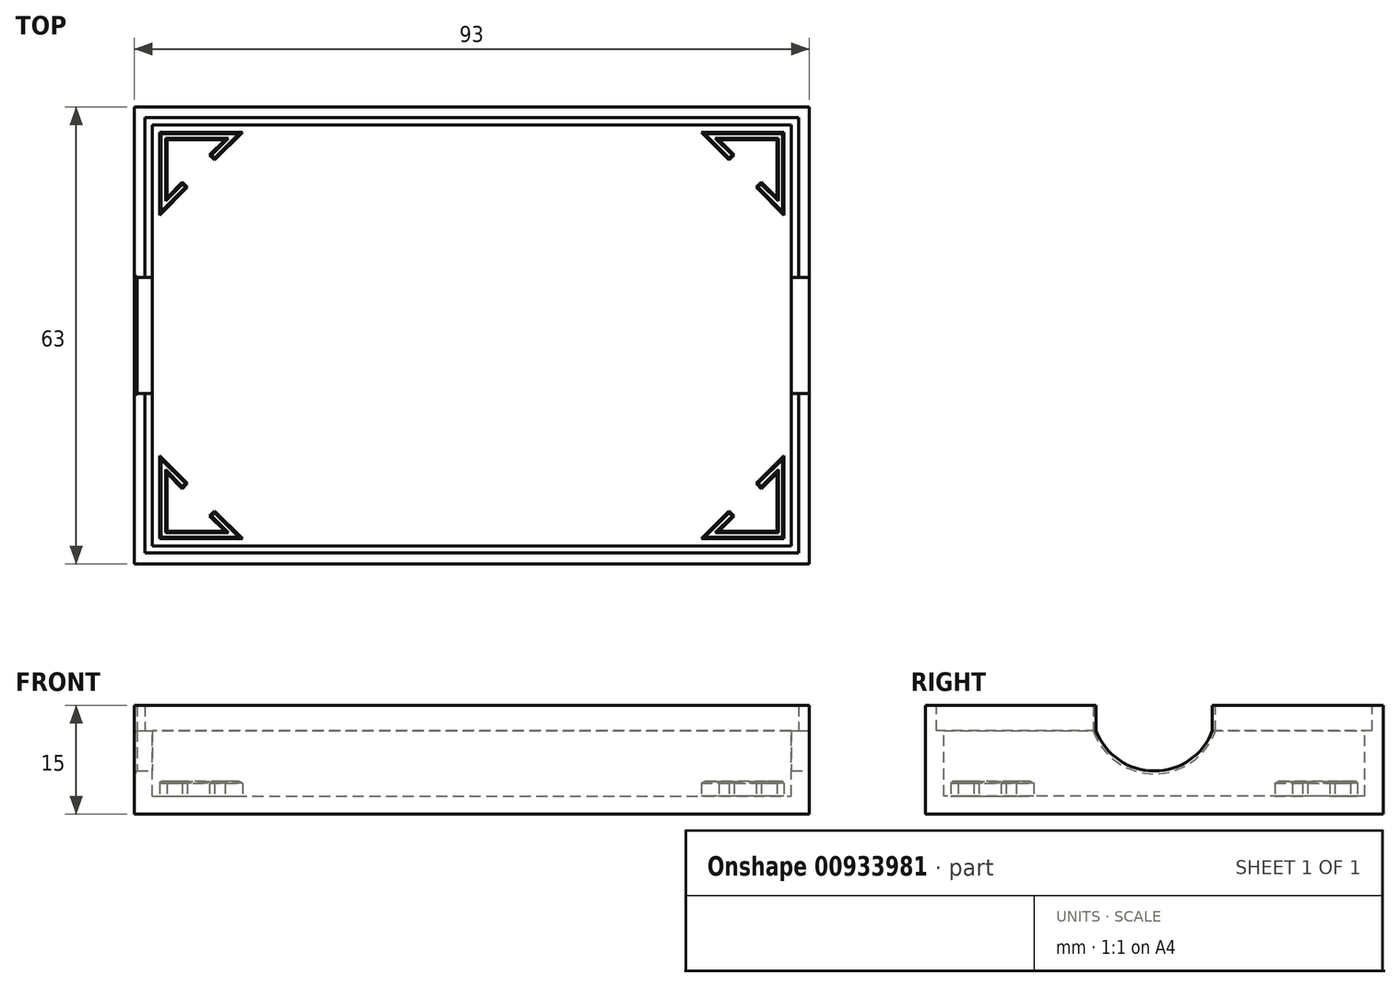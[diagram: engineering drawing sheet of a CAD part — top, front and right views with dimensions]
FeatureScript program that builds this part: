
annotation { "Feature Type Name" : "Feature", "Feature Type Description" : "" }
export const myFeature = defineFeature(function(context is Context, id is Id, definition is map)
    precondition{}
    {
        {
            var Q0;
            Q0=qCreatedBy(makeId("Top.planeOp"),FACE);
            var sketch = newSketch(context, id + "F0", { "sketchPlane" : qUnion([Q0])});
            skLineSegment(sketch, "E0.0", {"start": v(46.5, 31.5) * mm, "end": v(46.5, -31.5) * mm});
            skLineSegment(sketch, "E0.1", {"start": v(-46.5, 31.5) * mm, "end": v(46.5, 31.5) * mm});
            skLineSegment(sketch, "E0.2", {"start": v(-46.5, 31.5) * mm, "end": v(-46.5, -31.5) * mm});
            skLineSegment(sketch, "E0.3", {"start": v(-46.5, -31.5) * mm, "end": v(46.5, -31.5) * mm});
            skPoint(sketch, "E1", {"position": v(0, 31.5) * mm});
            skPoint(sketch, "E2", {"position": v(46.5, 0) * mm});
            skSolve(sketch);
        }
        {
            var Q0;
            Q0 = qSketchRegion(id + "F0", true);
            extrude(context, id + "F1", {"entities" : qUnion([Q0]), "oppositeDirection" : true, "depth" : 15 * mm, "offsetDistance" : 25 * mm});
        }
        {
            var Q0;
            Q0=makeQuery(id+"F1.opExtrude","CAP_FACE",FACE,{"disambiguationData":[OSD([sQuery(id+"F0.wireOp",EDGE,"E0.0"),sQuery(id+"F0.wireOp",EDGE,"E0.1"),sQuery(id+"F0.wireOp",EDGE,"E0.2"),sQuery(id+"F0.wireOp",EDGE,"E0.3")])],"isStart":true});
            shell(context, id + "F2", {"entities" : qUnion([Q0]), "thickness" : 2.5 * mm});
        }
        {
            var Q0;
            Q0=qCreatedBy(makeId("Top.planeOp"),FACE);
            var sketch = newSketch(context, id + "F3", { "sketchPlane" : qUnion([Q0])});
            skLineSegment(sketch, "E3.bottom", {"start": v(-45, 30) * mm, "end": v(45, 30) * mm});
            skLineSegment(sketch, "E3.top", {"start": v(-45, -30) * mm, "end": v(45, -30) * mm});
            skLineSegment(sketch, "E3.left", {"start": v(-45, 30) * mm, "end": v(-45, -30) * mm});
            skLineSegment(sketch, "E3.right", {"start": v(45, 30) * mm, "end": v(45, -30) * mm});
            skPoint(sketch, "E4", {"position": v(0, 30) * mm});
            skPoint(sketch, "E5", {"position": v(45, 0) * mm});
            skSolve(sketch);
        }
        {
            var Q0;
            Q0 = qSketchRegion(id + "F3", true);
            extrude(context, id + "F4", {"entities" : qUnion([Q0]), "operationType" : NewBodyOperationType.REMOVE, "oppositeDirection" : true, "depth" : 3.5 * mm, "offsetDistance" : 25 * mm});
        }
        {
            var Q0;
            Q0=makeQuery(id+"F2.opShell","OFFSET_FACE",FACE,{"disambiguationData":[OSD([sQuery(id+"F0.wireOp",EDGE,"E0.0"),sQuery(id+"F0.wireOp",EDGE,"E0.1"),sQuery(id+"F0.wireOp",EDGE,"E0.2"),sQuery(id+"F0.wireOp",EDGE,"E0.3")])]});
            var sketch = newSketch(context, id + "F5", { "sketchPlane" : qUnion([Q0])});
            skLineSegment(sketch, "E6.bottom", {"start": v(-42, 27) * mm, "end": v(-34, 27) * mm});
            skLineSegment(sketch, "E6.left", {"start": v(-42, 27) * mm, "end": v(-42, 19) * mm});
            skLineSegment(sketch, "E7", {"start": v(-42, 19) * mm, "end": v(-39.88, 21.12) * mm});
            skLineSegment(sketch, "E8.0", {"start": v(-43, 16.59) * mm, "end": v(-39.17, 20.41) * mm});
            skLineSegment(sketch, "E8.1", {"start": v(-43, 28) * mm, "end": v(-43, 16.59) * mm});
            skLineSegment(sketch, "E8.2", {"start": v(-43, 28) * mm, "end": v(-31.59, 28) * mm});
            skLineSegment(sketch, "E9.MirrorCS", {"start": v(42, 27) * mm, "end": v(34, 27) * mm});
            skLineSegment(sketch, "E10.MirrorCS", {"start": v(42, 27) * mm, "end": v(42, 19) * mm});
            skLineSegment(sketch, "E11.MirrorCS", {"start": v(43, 28) * mm, "end": v(43, 16.59) * mm});
            skLineSegment(sketch, "E12.MirrorCS", {"start": v(43, 28) * mm, "end": v(31.59, 28) * mm});
            skLineSegment(sketch, "E13.MirrorCS", {"start": v(-43, -28) * mm, "end": v(-31.59, -28) * mm});
            skLineSegment(sketch, "E14.MirrorCS", {"start": v(-42, -27) * mm, "end": v(-34, -27) * mm});
            skLineSegment(sketch, "E15.MirrorCS", {"start": v(-42, -27) * mm, "end": v(-42, -19) * mm});
            skLineSegment(sketch, "E16.MirrorCS", {"start": v(-43, -28) * mm, "end": v(-43, -16.59) * mm});
            skLineSegment(sketch, "E17.MirrorCS", {"start": v(43, -28) * mm, "end": v(31.59, -28) * mm});
            skLineSegment(sketch, "E18.MirrorCS", {"start": v(43, -28) * mm, "end": v(43, -16.59) * mm});
            skLineSegment(sketch, "E19.MirrorCS", {"start": v(42, -27) * mm, "end": v(42, -19) * mm});
            skLineSegment(sketch, "E20.MirrorCS", {"start": v(42, -27) * mm, "end": v(34, -27) * mm});
            skLineSegment(sketch, "E21", {"start": v(-39.88, 21.12) * mm, "end": v(-39.17, 20.41) * mm});
            skLineSegment(sketch, "E22", {"start": v(-36.12, 24.88) * mm, "end": v(-35.41, 24.17) * mm});
            skLineSegment(sketch, "E23.trimOffspring", {"start": v(-35.41, 24.17) * mm, "end": v(-31.59, 28) * mm});
            skLineSegment(sketch, "E24.trimOffspring", {"start": v(-36.12, 24.88) * mm, "end": v(-34, 27) * mm});
            skLineSegment(sketch, "E25.MirrorCS", {"start": v(35.41, 24.17) * mm, "end": v(31.59, 28) * mm});
            skLineSegment(sketch, "E26.MirrorCS", {"start": v(36.12, 24.88) * mm, "end": v(34, 27) * mm});
            skLineSegment(sketch, "E27.MirrorCS", {"start": v(36.12, 24.88) * mm, "end": v(35.41, 24.17) * mm});
            skLineSegment(sketch, "E28.MirrorCS", {"start": v(39.88, 21.12) * mm, "end": v(39.17, 20.41) * mm});
            skLineSegment(sketch, "E29.MirrorCS", {"start": v(42, 19) * mm, "end": v(39.88, 21.12) * mm});
            skLineSegment(sketch, "E30.MirrorCS", {"start": v(43, 16.59) * mm, "end": v(39.17, 20.41) * mm});
            skLineSegment(sketch, "E31.MirrorCS", {"start": v(-42, -19) * mm, "end": v(-39.88, -21.12) * mm});
            skLineSegment(sketch, "E32.MirrorCS", {"start": v(-39.88, -21.12) * mm, "end": v(-39.17, -20.41) * mm});
            skLineSegment(sketch, "E33.MirrorCS", {"start": v(-43, -16.59) * mm, "end": v(-39.17, -20.41) * mm});
            skLineSegment(sketch, "E34.MirrorCS", {"start": v(-36.12, -24.88) * mm, "end": v(-34, -27) * mm});
            skLineSegment(sketch, "E35.MirrorCS", {"start": v(-36.12, -24.88) * mm, "end": v(-35.41, -24.17) * mm});
            skLineSegment(sketch, "E36.MirrorCS", {"start": v(-35.41, -24.17) * mm, "end": v(-31.59, -28) * mm});
            skLineSegment(sketch, "E37.MirrorCS", {"start": v(42, -19) * mm, "end": v(39.88, -21.12) * mm});
            skLineSegment(sketch, "E38.MirrorCS", {"start": v(39.88, -21.12) * mm, "end": v(39.17, -20.41) * mm});
            skLineSegment(sketch, "E39.MirrorCS", {"start": v(43, -16.59) * mm, "end": v(39.17, -20.41) * mm});
            skLineSegment(sketch, "E40.MirrorCS", {"start": v(36.12, -24.88) * mm, "end": v(34, -27) * mm});
            skLineSegment(sketch, "E41.MirrorCS", {"start": v(35.41, -24.17) * mm, "end": v(31.59, -28) * mm});
            skLineSegment(sketch, "E42.MirrorCS", {"start": v(36.12, -24.88) * mm, "end": v(35.41, -24.17) * mm});
            skSolve(sketch);
        }
        {
            var Q0;
            Q0 = qSketchRegion(id + "F5", true);
            extrude(context, id + "F6", {"entities" : qUnion([Q0]), "operationType" : NewBodyOperationType.ADD, "depth" : 2 * mm, "offsetDistance" : 25 * mm});
        }
        {
            var Q0;
            Q0=makeQuery(id+"F6.opExtrude","CAP_FACE",FACE,{"disambiguationData":[OSD([sQuery(id+"F5.wireOp",EDGE,"E6.bottom"),sQuery(id+"F5.wireOp",EDGE,"E6.left"),sQuery(id+"F5.wireOp",EDGE,"E7"),sQuery(id+"F5.wireOp",EDGE,"E8.0"),sQuery(id+"F5.wireOp",EDGE,"E8.1"),sQuery(id+"F5.wireOp",EDGE,"E8.2")])],"isStart":false});
            var Q1;
            Q1=makeQuery(id+"F6.opExtrude","CAP_FACE",FACE,{"disambiguationData":[OSD([sQuery(id+"F5.wireOp",EDGE,"7368ef62-361c-4206-994a-d8a41f0acc9b0.MirrorCS"),sQuery(id+"F5.wireOp",EDGE,"065983df-0b87-484f-8e97-a6bd623cd0b60.MirrorCS"),sQuery(id+"F5.wireOp",EDGE,"E9.MirrorCS"),sQuery(id+"F5.wireOp",EDGE,"E10.MirrorCS"),sQuery(id+"F5.wireOp",EDGE,"E11.MirrorCS"),sQuery(id+"F5.wireOp",EDGE,"E12.MirrorCS")])],"isStart":false});
            var Q2;
            Q2=makeQuery(id+"F6.opExtrude","CAP_FACE",FACE,{"disambiguationData":[OSD([sQuery(id+"F5.wireOp",EDGE,"cfee1d1f-dcdf-40e0-b635-4211958b80790.MirrorCS"),sQuery(id+"F5.wireOp",EDGE,"2ad0a4fe-2727-4fc3-9ba8-781443fbefe10.MirrorCS"),sQuery(id+"F5.wireOp",EDGE,"E17.MirrorCS"),sQuery(id+"F5.wireOp",EDGE,"E18.MirrorCS"),sQuery(id+"F5.wireOp",EDGE,"E19.MirrorCS"),sQuery(id+"F5.wireOp",EDGE,"E20.MirrorCS")])],"isStart":false});
            var Q3;
            Q3=makeQuery(id+"F6.opExtrude","CAP_FACE",FACE,{"disambiguationData":[OSD([sQuery(id+"F5.wireOp",EDGE,"E13.MirrorCS"),sQuery(id+"F5.wireOp",EDGE,"E14.MirrorCS"),sQuery(id+"F5.wireOp",EDGE,"E15.MirrorCS"),sQuery(id+"F5.wireOp",EDGE,"E16.MirrorCS"),sQuery(id+"F5.wireOp",EDGE,"85b368af-3590-4ccb-beb0-d535ae87f27b0.MirrorCS"),sQuery(id+"F5.wireOp",EDGE,"bbde580a-0e57-42fd-9440-816c3c4a825d0.MirrorCS")])],"isStart":false});
            chamfer(context, id + "F7", {"entities" : qUnion([Q0, Q1, Q2, Q3]), "width" : 0.2 * mm, "tangentPropagation" : true});
        }
        {
            var Q0;
            Q0=makeQuery(id+"F1.opExtrude","SWEPT_FACE",FACE,{"disambiguationData":[OSD([sQuery(id+"F0.wireOp",EDGE,"E0.0")])]});
            var sketch = newSketch(context, id + "F8", { "sketchPlane" : qUnion([Q0])});
            skPoint(sketch, "E43", {"position": v(-8, 0) * mm});
            skPoint(sketch, "E44", {"position": v(8, 0) * mm});
            skPoint(sketch, "E45", {"position": v(-8, -3.5) * mm});
            skPoint(sketch, "E46", {"position": v(8, -3.5) * mm});
            skArc(sketch, "E47", {"start": v(-8, -3.5) * mm, "mid": v(0, -9.04) * mm, "end": v(8, -3.5) * mm});
            skLineSegment(sketch, "E48", {"start": v(-8, 0) * mm, "end": v(0, 0) * mm});
            skLineSegment(sketch, "E49", {"start": v(0, 0) * mm, "end": v(8, 0) * mm});
            skLineSegment(sketch, "E50", {"start": v(8, -3.5) * mm, "end": v(8, 0) * mm});
            skLineSegment(sketch, "E51", {"start": v(-8, 0) * mm, "end": v(-8, -3.5) * mm});
            skSolve(sketch);
        }
        {
            var Q0;
            Q0 = qSketchRegion(id + "F8", true);
            extrude(context, id + "F9", {"entities" : qUnion([Q0]), "operationType" : NewBodyOperationType.REMOVE, "endBound" : BoundingType.THROUGH_ALL, "oppositeDirection" : true, "depth" : 25 * mm, "offsetDistance" : 25 * mm});
        }
        {
            var Q0;
            Q0=makeQuery(id+"F9.boolean.opBoolean","COPY",EDGE,{"derivedFrom":makeQuery(id+"F9.opExtrude","CAP_EDGE",EDGE,{"disambiguationData":[OSD([sQuery(id+"F8.wireOp",EDGE,"E47")])],"isStart":true})});
            var Q1;
            Q1=makeQuery(id+"F9.boolean.opBoolean","COPY",EDGE,{"derivedFrom":makeQuery(id+"F9.opExtrude","CAP_EDGE",EDGE,{"disambiguationData":[OSD([sQuery(id+"F8.wireOp",EDGE,"E50")])],"isStart":true})});
            var Q2;
            Q2=makeQuery(id+"F9.boolean.opBoolean","COPY",EDGE,{"derivedFrom":makeQuery(id+"F9.opExtrude","CAP_EDGE",EDGE,{"disambiguationData":[OSD([sQuery(id+"F8.wireOp",EDGE,"E51")])],"isStart":true})});
            var Q3;
            Q3=makeQuery(id+"F9.boolean.opBoolean","INTERSECT",EDGE,{"derivedFrom":[makeQuery(id+"F1.opExtrude","SWEPT_FACE",FACE,{"disambiguationData":[OSD([sQuery(id+"F0.wireOp",EDGE,"E0.2")])]}),makeQuery(id+"F9.opExtrude","SWEPT_FACE",FACE,{"disambiguationData":[OSD([sQuery(id+"F8.wireOp",EDGE,"E50")])]})]});
            var Q4;
            Q4=makeQuery(id+"F9.boolean.opBoolean","INTERSECT",EDGE,{"derivedFrom":[makeQuery(id+"F1.opExtrude","SWEPT_FACE",FACE,{"disambiguationData":[OSD([sQuery(id+"F0.wireOp",EDGE,"E0.2")])]}),makeQuery(id+"F9.opExtrude","SWEPT_FACE",FACE,{"disambiguationData":[OSD([sQuery(id+"F8.wireOp",EDGE,"E47")])]})]});
            var Q5;
            Q5=makeQuery(id+"F9.boolean.opBoolean","INTERSECT",EDGE,{"derivedFrom":[makeQuery(id+"F1.opExtrude","SWEPT_FACE",FACE,{"disambiguationData":[OSD([sQuery(id+"F0.wireOp",EDGE,"E0.2")])]}),makeQuery(id+"F9.opExtrude","SWEPT_FACE",FACE,{"disambiguationData":[OSD([sQuery(id+"F8.wireOp",EDGE,"E51")])]})]});
            chamfer(context, id + "F10", {"entities" : qUnion([Q0, Q1, Q2, Q3, Q4, Q5]), "width" : 0.4 * mm, "tangentPropagation" : true});
        }
    });
